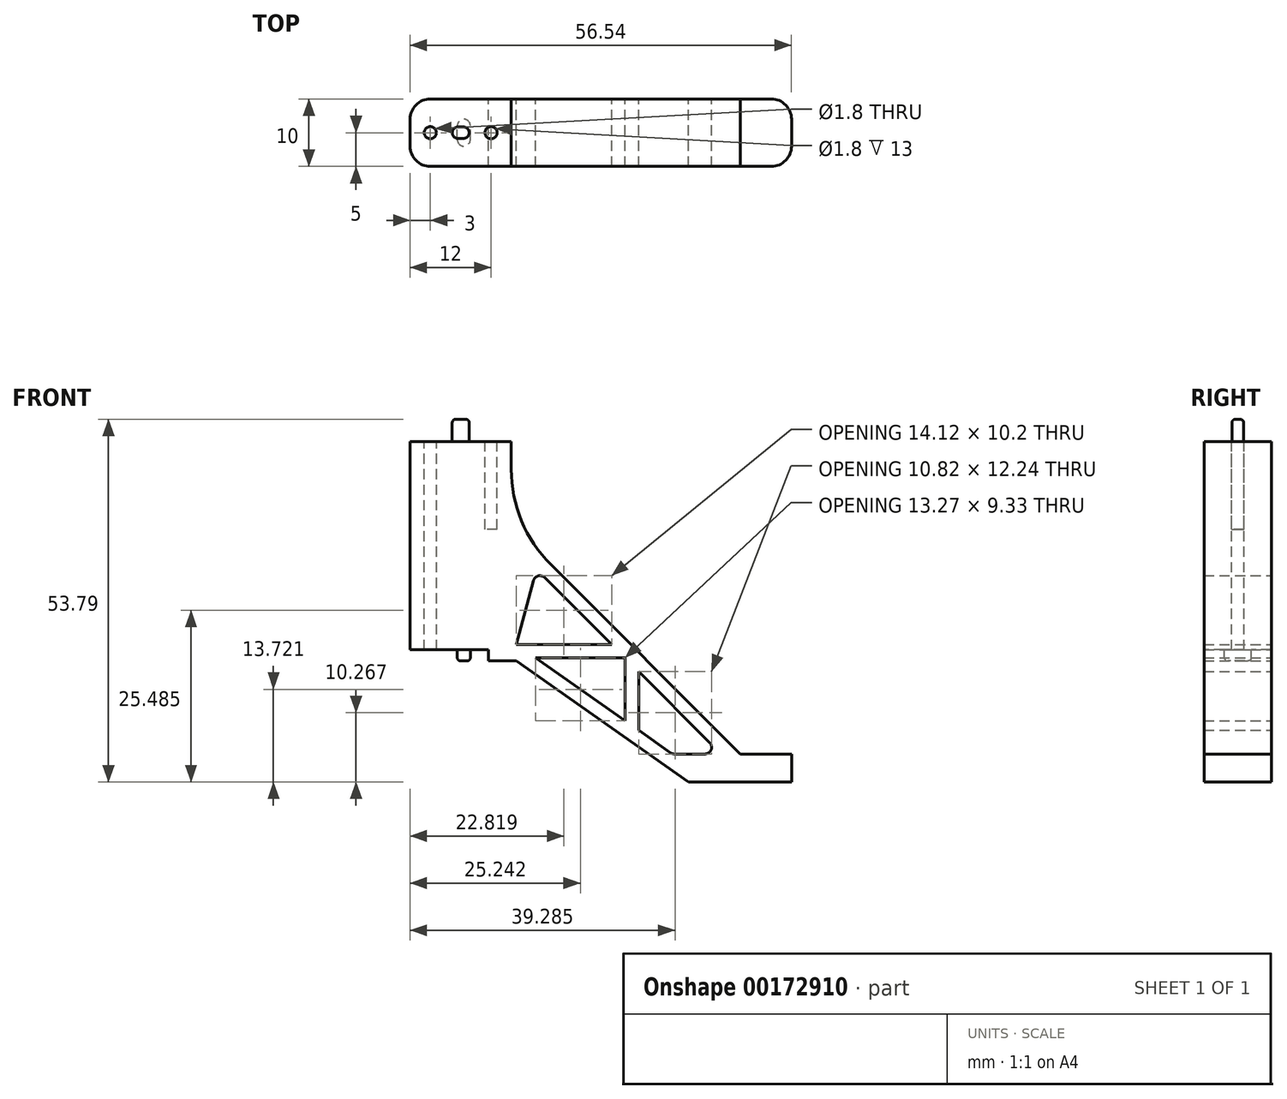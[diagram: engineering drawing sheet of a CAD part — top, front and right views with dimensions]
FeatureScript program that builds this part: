
annotation { "Feature Type Name" : "Feature", "Feature Type Description" : "" }
export const myFeature = defineFeature(function(context is Context, id is Id, definition is map)
    precondition{}
    {
        {
            var Q0;
            Q0=qCreatedBy(makeId("Front.planeOp"),FACE);
            var sketch = newSketch(context, id + "F0", { "sketchPlane" : qUnion([Q0])});
            skLineSegment(sketch, "E0", {"start": v(0, 30.9) * mm, "end": v(15, 30.9) * mm});
            skLineSegment(sketch, "E1", {"start": v(15, 30.9) * mm, "end": v(15, 18.5) * mm});
            skLineSegment(sketch, "E2", {"start": v(15, 18.5) * mm, "end": v(48.94, -15.44) * mm});
            skLineSegment(sketch, "E3", {"start": v(48.94, -15.44) * mm, "end": v(56.54, -15.44) * mm});
            skLineSegment(sketch, "E4", {"start": v(56.54, -15.44) * mm, "end": v(56.54, -19.6) * mm});
            skLineSegment(sketch, "E5", {"start": v(56.54, -19.6) * mm, "end": v(41.3, -19.6) * mm});
            skLineSegment(sketch, "E6", {"start": v(41.3, -19.6) * mm, "end": v(15.76, -1.65) * mm});
            skLineSegment(sketch, "E7", {"start": v(0, 0) * mm, "end": v(0, 30.9) * mm});
            skLineSegment(sketch, "E8", {"start": v(0, 0) * mm, "end": v(11.6, 0) * mm});
            skLineSegment(sketch, "E9", {"start": v(11.6, 0) * mm, "end": v(11.6, -1.65) * mm});
            skLineSegment(sketch, "E10", {"start": v(11.6, -1.65) * mm, "end": v(15.76, -1.65) * mm});
            skLineSegment(sketch, "E11", {"start": v(15.76, 0.8) * mm, "end": v(29.88, 0.8) * mm});
            skLineSegment(sketch, "E12", {"start": v(29.88, 0.8) * mm, "end": v(19.97, 10.7) * mm});
            skLineSegment(sketch, "E13", {"start": v(18.3, 10.26) * mm, "end": v(15.76, 0.8) * mm});
            skLineSegment(sketch, "E14", {"start": v(18.6, -1.2) * mm, "end": v(31.88, -1.2) * mm});
            skLineSegment(sketch, "E15", {"start": v(31.88, -1.2) * mm, "end": v(31.88, -10.53) * mm});
            skLineSegment(sketch, "E16", {"start": v(31.88, -10.53) * mm, "end": v(18.6, -1.2) * mm});
            skLineSegment(sketch, "E17", {"start": v(33.88, -3.2) * mm, "end": v(33.88, -11.94) * mm});
            skLineSegment(sketch, "E18", {"start": v(33.88, -11.94) * mm, "end": v(38.6, -15.26) * mm});
            skLineSegment(sketch, "E19", {"start": v(39.18, -15.44) * mm, "end": v(43.7, -15.44) * mm});
            skLineSegment(sketch, "E20", {"start": v(44.4, -13.73) * mm, "end": v(33.88, -3.2) * mm});
            skPoint(sketch, "E21.visualSharp", {"position": v(18.74, 11.93) * mm});
            skArc(sketch, "E21.filletArc", {"start": v(19.97, 10.7) * mm, "mid": v(19, 10.96) * mm, "end": v(18.3, 10.26) * mm});
            skPoint(sketch, "E22.visualSharp", {"position": v(46.11, -15.44) * mm});
            skArc(sketch, "E22.filletArc", {"start": v(43.7, -15.44) * mm, "mid": v(44.62, -14.82) * mm, "end": v(44.4, -13.73) * mm});
            skPoint(sketch, "E23.visualSharp", {"position": v(38.86, -15.44) * mm});
            skArc(sketch, "E23.filletArc", {"start": v(38.6, -15.26) * mm, "mid": v(38.88, -15.4) * mm, "end": v(39.18, -15.44) * mm});
            skSolve(sketch);
        }
        {
            var Q0;
            Q0 = qSketchRegion(id + "F0", true);
            extrude(context, id + "F1", {"entities" : qUnion([Q0]), "endBound" : BoundingType.SYMMETRIC, "depth" : 10 * mm, "hasSecondDirection" : true, "secondDirectionOppositeDirection" : true, "secondDirectionDepth" : 25 * mm});
        }
        {
            var Q0;
            Q0=makeQuery(id+"F1.opExtrude","SWEPT_FACE",FACE,{"disambiguationData":[OSD([sQuery(id+"F0.wireOp",EDGE,"E0")])]});
            var sketch = newSketch(context, id + "F2", { "sketchPlane" : qUnion([Q0])});
            skCircle(sketch, "E24", {"center": v(3, 0) * mm, "radius": 0.9 * mm});
            skCircle(sketch, "E25", {"center": v(12, 0) * mm, "radius": 0.9 * mm});
            skSolve(sketch);
        }
        {
            var Q0;
            Q0=makeQuery(id+"F2.imprint","IMPRINT",FACE,{"disambiguationData":[TD([[makeQuery(id+"F2.imprint","IMPRINT",EDGE,{"derivedFrom":sQuery(id+"F2.wireOp",EDGE,"E24")}),1.0]])]});
            extrude(context, id + "F3", {"entities" : qUnion([Q0]), "operationType" : NewBodyOperationType.REMOVE, "endBound" : BoundingType.THROUGH_ALL, "oppositeDirection" : true, "depth" : 25 * mm});
        }
        {
            var Q0;
            Q0=makeQuery(id+"F2.imprint","IMPRINT",FACE,{"disambiguationData":[TD([[makeQuery(id+"F2.imprint","IMPRINT",EDGE,{"derivedFrom":sQuery(id+"F2.wireOp",EDGE,"E25")}),1.0]])]});
            extrude(context, id + "F4", {"entities" : qUnion([Q0]), "operationType" : NewBodyOperationType.REMOVE, "oppositeDirection" : true, "depth" : 13 * mm});
        }
        {
            var Q0;
            Q0=makeQuery(id+"F1.opExtrude","SWEPT_FACE",FACE,{"disambiguationData":[OSD([sQuery(id+"F0.wireOp",EDGE,"E0")])]});
            var sketch = newSketch(context, id + "F5", { "sketchPlane" : qUnion([Q0])});
            skArc(sketch, "E26", {"start": v(7.1, 0.86) * mm, "mid": v(6.25, 0) * mm, "end": v(7.1, -0.86) * mm});
            skArc(sketch, "E27", {"start": v(7.89, -0.86) * mm, "mid": v(8.75, 0) * mm, "end": v(7.89, 0.86) * mm});
            skLineSegment(sketch, "E28.bottom", {"start": v(7.1, 0.86) * mm, "end": v(7.89, 0.86) * mm});
            skLineSegment(sketch, "E28.top", {"start": v(7.1, -0.86) * mm, "end": v(7.89, -0.86) * mm});
            skLineSegment(sketch, "E29", {"start": v(7.5, 0.86) * mm, "end": v(7.5, -0.86) * mm, "construction": true});
            skSolve(sketch);
        }
        {
            var Q0;
            Q0=makeQuery(id+"F5.imprint","IMPRINT",FACE,{"disambiguationData":[TD([[makeQuery(id+"F5.imprint","IMPRINT",EDGE,{"derivedFrom":sQuery(id+"F5.wireOp",EDGE,"E26")}),1.0]])]});
            extrude(context, id + "F6", {"entities" : qUnion([Q0]), "operationType" : NewBodyOperationType.ADD, "depth" : 3.3 * mm});
        }
        {
            var Q0;
            Q0=makeQuery(id+"F1.opExtrude","SWEPT_FACE",FACE,{"disambiguationData":[OSD([sQuery(id+"F0.wireOp",EDGE,"E8")])]});
            var sketch = newSketch(context, id + "F7", { "sketchPlane" : qUnion([Q0])});
            skArc(sketch, "E30", {"start": v(8.93, 1.03) * mm, "mid": v(7.96, 2) * mm, "end": v(7, 1.04) * mm});
            skArc(sketch, "E31", {"start": v(7, -1.04) * mm, "mid": v(7.96, -2) * mm, "end": v(8.93, -1.03) * mm});
            skLineSegment(sketch, "E32", {"start": v(8.93, 1.03) * mm, "end": v(8.93, -1.03) * mm});
            skLineSegment(sketch, "E33", {"start": v(7, 1.04) * mm, "end": v(7, -1.04) * mm});
            skSolve(sketch);
        }
        {
            var Q0;
            Q0 = qSketchRegion(id + "F7", true);
            var Q1;
            Q1=makeQuery(id+"F1.opExtrude","SWEPT_FACE",FACE,{"disambiguationData":[OSD([sQuery(id+"F0.wireOp",EDGE,"E10")])]});
            extrude(context, id + "F8", {"entities" : qUnion([Q0]), "operationType" : NewBodyOperationType.ADD, "endBound" : BoundingType.UP_TO_SURFACE, "endBoundEntityFace" : qUnion([Q1]), "depth" : 25 * mm});
        }
        {
            var Q0;
            Q0=makeQuery(id+"F6.opExtrude","CAP_FACE",FACE,{"disambiguationData":[OSD([sQuery(id+"F5.wireOp",EDGE,"E26"),sQuery(id+"F5.wireOp",EDGE,"E27"),sQuery(id+"F5.wireOp",EDGE,"E28.bottom"),sQuery(id+"F5.wireOp",EDGE,"E28.top")])],"isStart":false});
            var Q1;
            Q1=makeQuery(id+"F8.opExtrude","CAP_FACE",FACE,{"disambiguationData":[OSD([sQuery(id+"F7.wireOp",EDGE,"E30"),sQuery(id+"F7.wireOp",EDGE,"E31"),sQuery(id+"F7.wireOp",EDGE,"E32"),sQuery(id+"F7.wireOp",EDGE,"E33")])],"isStart":false});
            fillet(context, id + "F9", {"entities" : qUnion([Q0, Q1]), "radius" : .5 * mm, "tangentPropagation" : true, "allowEdgeOverflow" : false});
        }
        {
            var Q0;
            Q0=makeQuery(id+"F1.opExtrude","CAP_EDGE",EDGE,{"disambiguationData":[OSD([sQuery(id+"F0.wireOp",EDGE,"E7")])],"isStart":false});
            var Q1;
            Q1=makeQuery(id+"F1.opExtrude","CAP_EDGE",EDGE,{"disambiguationData":[OSD([sQuery(id+"F0.wireOp",EDGE,"E7")])],"isStart":true});
            var Q2;
            Q2=makeQuery(id+"F1.opExtrude","CAP_EDGE",EDGE,{"disambiguationData":[OSD([sQuery(id+"F0.wireOp",EDGE,"E4")])],"isStart":false});
            var Q3;
            Q3=makeQuery(id+"F1.opExtrude","CAP_EDGE",EDGE,{"disambiguationData":[OSD([sQuery(id+"F0.wireOp",EDGE,"E4")])],"isStart":true});
            fillet(context, id + "F10", {"entities" : qUnion([Q0, Q1, Q2, Q3]), "radius" : 3 * mm, "tangentPropagation" : true, "allowEdgeOverflow" : false});
        }
        {
            var Q0;
            Q0=makeQuery(id+"F1.opExtrude","SWEPT_EDGE",EDGE,{"disambiguationData":[OSD([sQuery(id+"F0.wireOp",EDGE,"E1"),sQuery(id+"F0.wireOp",EDGE,"E2")])]});
            fillet(context, id + "F11", {"entities" : qUnion([Q0]), "radius" : 20 * mm, "tangentPropagation" : true, "allowEdgeOverflow" : false});
        }
    });
